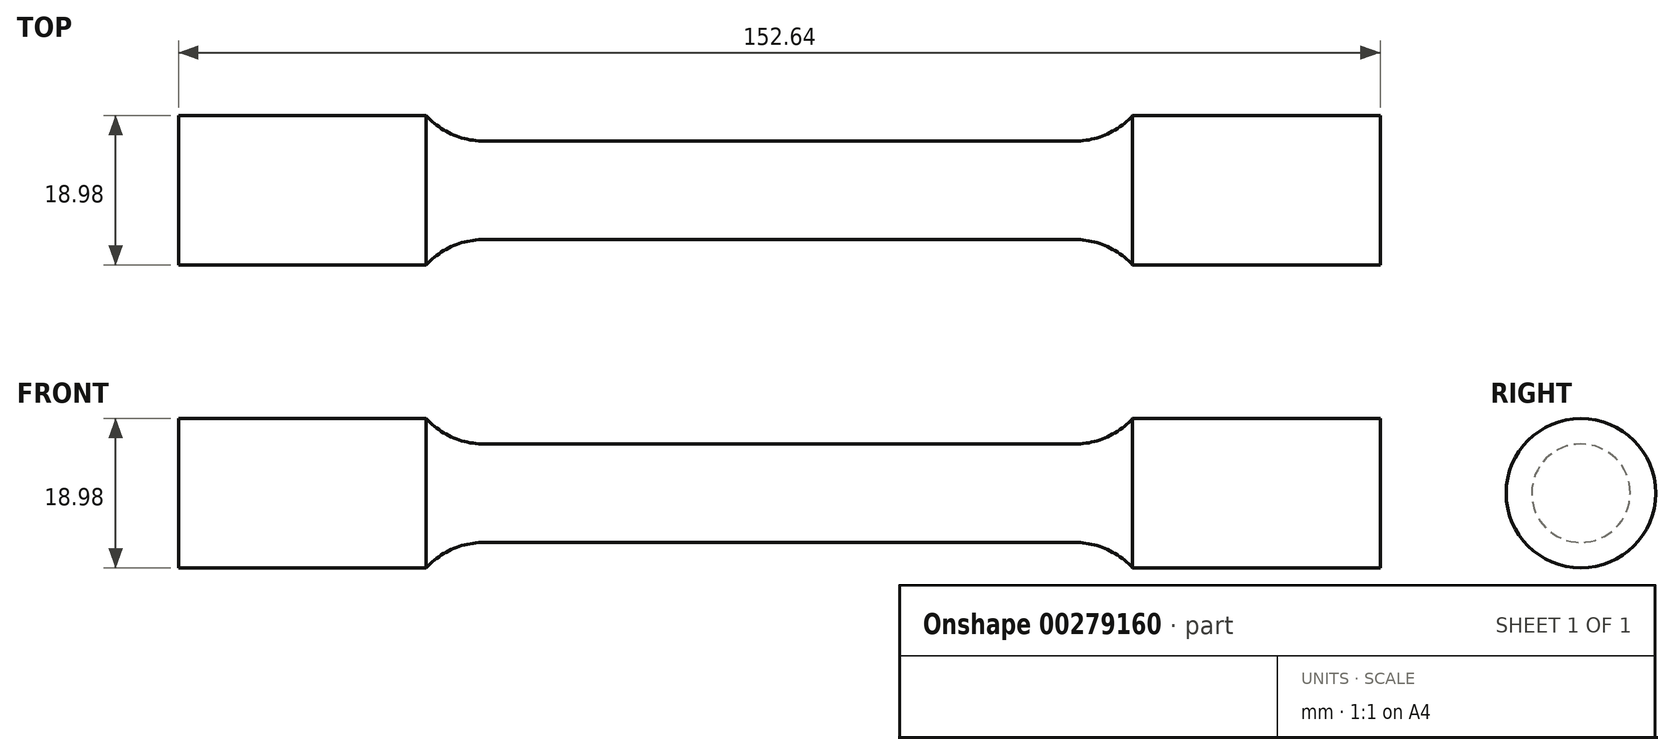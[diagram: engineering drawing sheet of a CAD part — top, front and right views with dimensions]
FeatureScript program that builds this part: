
annotation { "Feature Type Name" : "Feature", "Feature Type Description" : "" }
export const myFeature = defineFeature(function(context is Context, id is Id, definition is map)
    precondition{}
    {
        {
            var Q0;
            Q0=qCreatedBy(makeId("Front.planeOp"),FACE);
            var sketch = newSketch(context, id + "F0", { "sketchPlane" : qUnion([Q0])});
            skLineSegment(sketch, "E0", {"start": v(0, 6.25) * mm, "end": v(37.5, 6.25) * mm});
            skArc(sketch, "E1", {"start": v(37.5, 6.25) * mm, "mid": v(41.53, 7.1) * mm, "end": v(44.87, 9.5) * mm});
            skLineSegment(sketch, "E2", {"start": v(44.87, 9.5) * mm, "end": v(76.32, 9.5) * mm});
            skLineSegment(sketch, "E3", {"start": v(76.32, 9.5) * mm, "end": v(76.32, 0) * mm});
            skArc(sketch, "E4.MirrorCS", {"start": v(-37.5, 6.25) * mm, "mid": v(-41.53, 7.1) * mm, "end": v(-44.87, 9.5) * mm});
            skLineSegment(sketch, "E5.MirrorCS", {"start": v(0, 6.25) * mm, "end": v(-37.5, 6.25) * mm});
            skLineSegment(sketch, "E6.MirrorCS", {"start": v(-76.32, 9.5) * mm, "end": v(-76.32, 0) * mm});
            skLineSegment(sketch, "E7.MirrorCS", {"start": v(-44.87, 9.5) * mm, "end": v(-76.32, 9.5) * mm});
            skLineSegment(sketch, "E8", {"start": v(-76.32, 0) * mm, "end": v(76.32, 0) * mm});
            skSolve(sketch);
        }
        {
            var Q0;
            Q0 = qSketchRegion(id + "F0", true);
            var Q1;
            Q1=sQuery(id+"F0.wireOp",EDGE,"E8");
            revolve(context, id + "F1", {"entities" : qUnion([Q0]), "axis" : qUnion([Q1]), "revolveType" : RevolveType.FULL});
        }
    });
